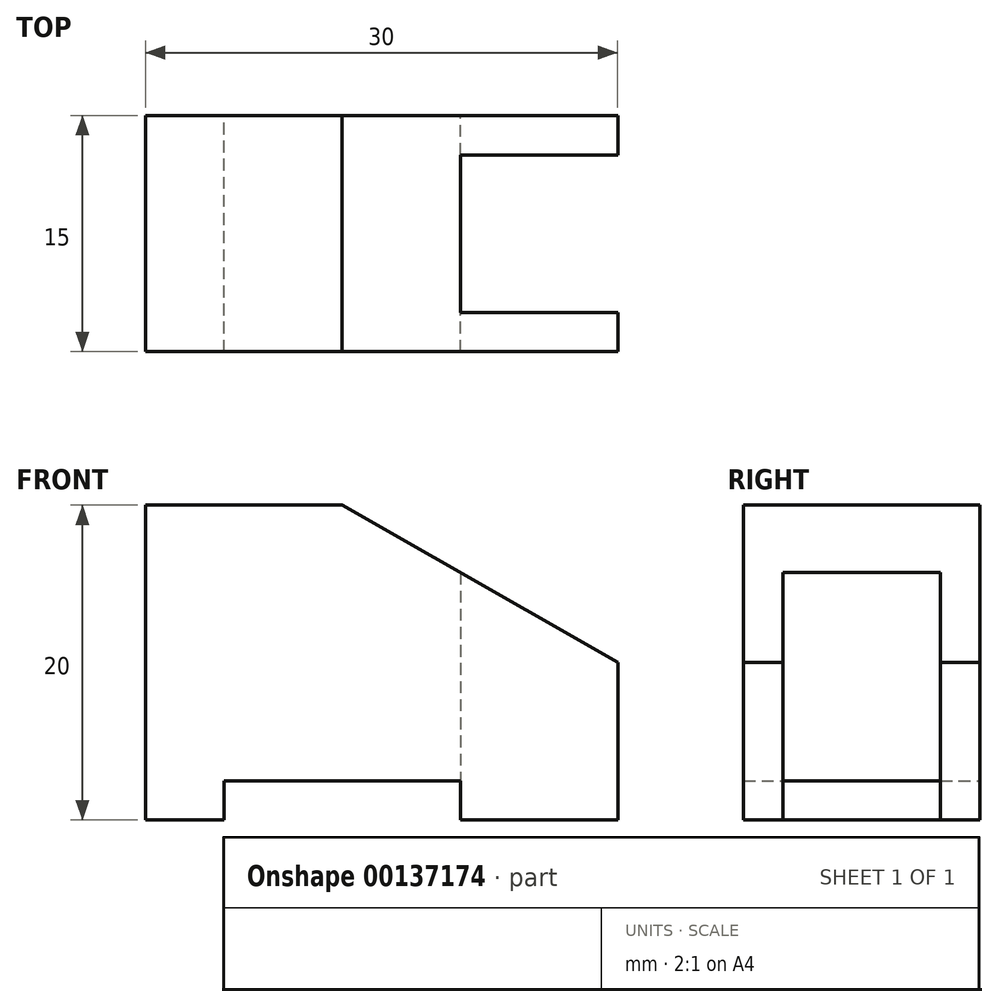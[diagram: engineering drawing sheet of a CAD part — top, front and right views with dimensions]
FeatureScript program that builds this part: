
annotation { "Feature Type Name" : "Feature", "Feature Type Description" : "" }
export const myFeature = defineFeature(function(context is Context, id is Id, definition is map)
    precondition{}
    {
        {
            var Q0;
            Q0=qCreatedBy(makeId("Front.planeOp"),FACE);
            var sketch = newSketch(context, id + "F0", { "sketchPlane" : qUnion([Q0])});
            skLineSegment(sketch, "E0.left", {"start": v(-14.03, 0) * mm, "end": v(-14.03, 20) * mm});
            skLineSegment(sketch, "E1", {"start": v(-14.03, 20) * mm, "end": v(-1.53, 20) * mm});
            skLineSegment(sketch, "E2", {"start": v(15.97, 0) * mm, "end": v(15.97, 10) * mm});
            skLineSegment(sketch, "E3", {"start": v(-1.53, 20) * mm, "end": v(15.97, 10) * mm});
            skLineSegment(sketch, "E4", {"start": v(-14.03, 0) * mm, "end": v(-9.03, 0) * mm});
            skLineSegment(sketch, "E5", {"start": v(15.97, 0) * mm, "end": v(5.97, 0) * mm});
            skLineSegment(sketch, "E6", {"start": v(5.97, 0) * mm, "end": v(5.97, 2.5) * mm});
            skLineSegment(sketch, "E7", {"start": v(5.97, 2.5) * mm, "end": v(-9.03, 2.5) * mm});
            skLineSegment(sketch, "E8", {"start": v(-9.03, 2.5) * mm, "end": v(-9.03, 0) * mm});
            skSolve(sketch);
        }
        {
            var Q0;
            Q0 = qSketchRegion(id + "F0", true);
            extrude(context, id + "F1", {"entities" : qUnion([Q0]), "depth" : 15 * mm});
        }
        {
            var Q0;
            Q0=qCreatedBy(makeId("Top.planeOp"),FACE);
            var sketch = newSketch(context, id + "F2", { "sketchPlane" : qUnion([Q0])});
            skLineSegment(sketch, "E9.0", {"start": v(15.97, -15) * mm, "end": v(15.97, 0) * mm});
            skLineSegment(sketch, "E10", {"start": v(15.97, -2.5) * mm, "end": v(5.97, -2.5) * mm});
            skLineSegment(sketch, "E11", {"start": v(5.97, -2.5) * mm, "end": v(5.97, -12.5) * mm});
            skLineSegment(sketch, "E12", {"start": v(5.97, -12.5) * mm, "end": v(15.97, -12.5) * mm});
            skSolve(sketch);
        }
        {
            var Q0;
            Q0 = qSketchRegion(id + "F2", true);
            extrude(context, id + "F3", {"entities" : qUnion([Q0]), "operationType" : NewBodyOperationType.REMOVE, "depth" : 25 * mm});
        }
    });
